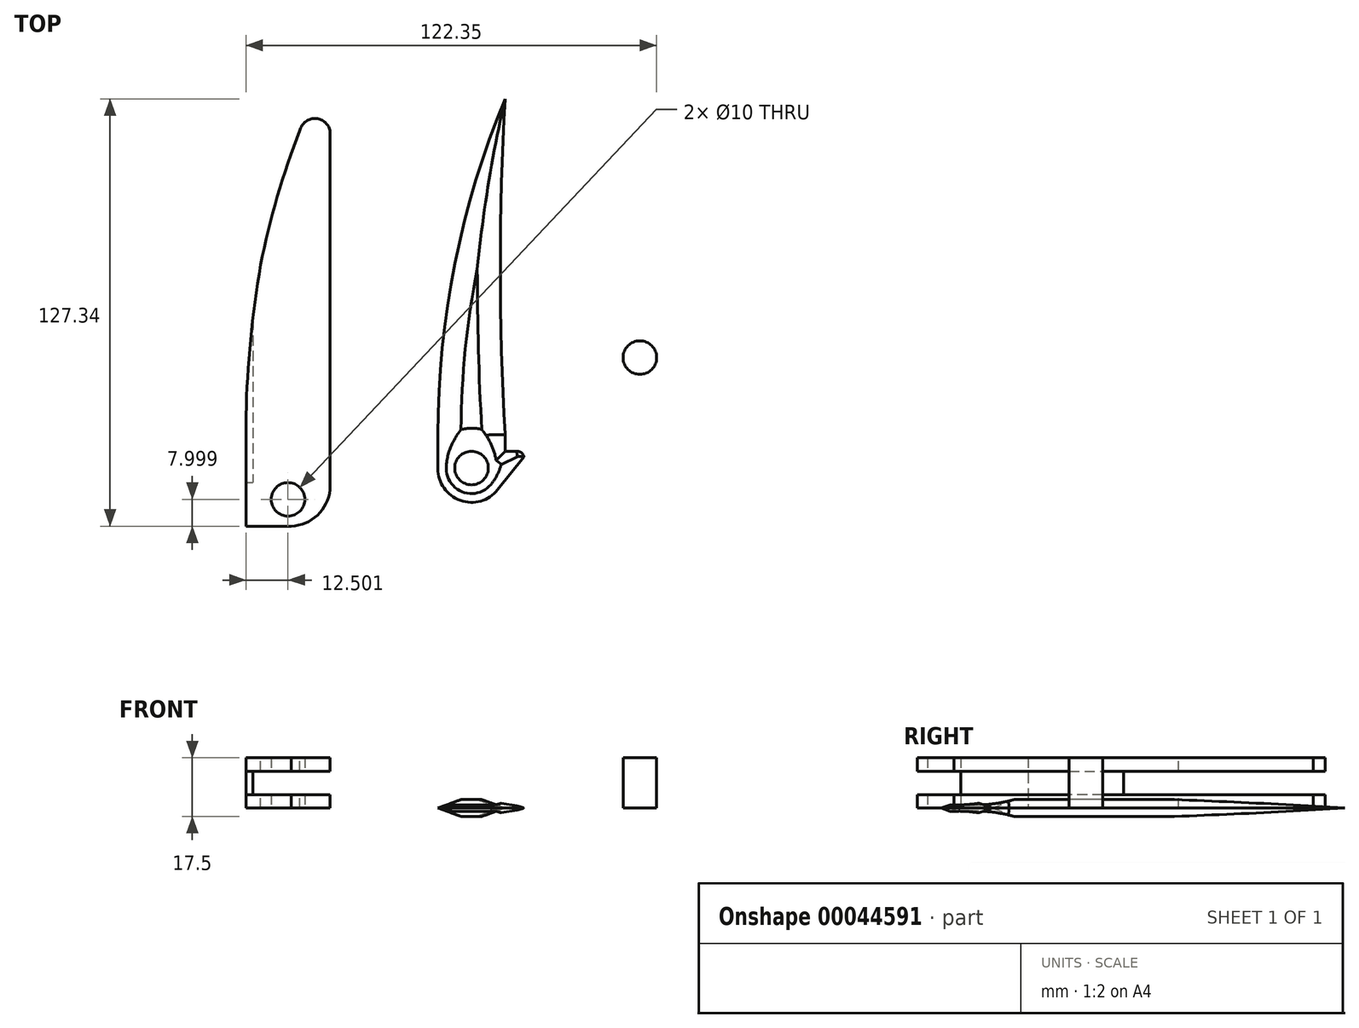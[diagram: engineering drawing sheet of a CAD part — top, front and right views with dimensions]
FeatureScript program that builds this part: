
annotation { "Feature Type Name" : "Feature", "Feature Type Description" : "" }
export const myFeature = defineFeature(function(context is Context, id is Id, definition is map)
    precondition{}
    {
        {
            var Q0;
            Q0=qCreatedBy(makeId("Top.planeOp"),FACE);
            var sketch = newSketch(context, id + "F0", { "sketchPlane" : qUnion([Q0])});
            skLineSegment(sketch, "E0.left", {"start": v(0, 0) * mm, "end": v(0, -5) * mm});
            skLineSegment(sketch, "E0.right", {"start": v(-20, 0) * mm, "end": v(-20, -10.3) * mm});
            skCircle(sketch, "E1", {"center": v(-10, -10) * mm, "radius": 5 * mm});
            skArc(sketch, "E2", {"start": v(-20, 0) * mm, "mid": v(-14.95, 51) * mm, "end": v(0, 100) * mm});
            skArc(sketch, "E3", {"start": v(0, 100) * mm, "mid": v(-1.43, 50) * mm, "end": v(0, 0) * mm});
            skArc(sketch, "E4", {"start": v(-20, -10.16) * mm, "mid": v(-13.34, -19.66) * mm, "end": v(-2.2, -16.48) * mm});
            skLineSegment(sketch, "E5", {"start": v(0, -5) * mm, "end": v(3.75, -5) * mm});
            skLineSegment(sketch, "E6", {"start": v(5.63, -6.7) * mm, "end": v(-2.2, -16.48) * mm});
            skArc(sketch, "E7", {"start": v(5.63, -6.7) * mm, "mid": v(4.9, -5.44) * mm, "end": v(3.5, -5) * mm});
            skPoint(sketch, "E8.orphan", {"position": v(7, -5) * mm});
            skPoint(sketch, "E9.orphan", {"position": v(-20, -20.33) * mm});
            skPoint(sketch, "E10.trimOffspring.end.orphan", {"position": v(0, -10) * mm});
            skPoint(sketch, "E11.trimOffspring.end.orphan", {"position": v(0, -20) * mm});
            skSolve(sketch);
        }
        {
            var Q0;
            Q0=qCreatedBy(makeId("Top.planeOp"),FACE);
            var sketch = newSketch(context, id + "F1", { "sketchPlane" : qUnion([Q0])});
            skLineSegment(sketch, "E12.bottom", {"start": v(-52.19, -34.34) * mm, "end": v(-77.19, -34.34) * mm});
            skLineSegment(sketch, "E12.top", {"start": v(-52.19, 85.66) * mm, "end": v(-77.19, 85.66) * mm});
            skLineSegment(sketch, "E12.left", {"start": v(-52.19, -34.34) * mm, "end": v(-52.19, 85.66) * mm});
            skLineSegment(sketch, "E12.right", {"start": v(-77.19, -34.34) * mm, "end": v(-77.19, 85.66) * mm});
            skCircle(sketch, "E13", {"center": v(-64.69, -19.34) * mm, "radius": 5 * mm});
            skArc(sketch, "E14", {"start": v(-64.69, 85.66) * mm, "mid": v(-74.63, 38.64) * mm, "end": v(-77.19, -9.34) * mm});
            skSolve(sketch);
        }
        {
            var Q0;
            {var subQ4=sQuery(id+"F1.wireOp",EDGE,"E12.bottom");Q0=makeQuery(id+"F1.imprint","IMPRINT",FACE,{"disambiguationData":[TD([[makeQuery(id+"F1.imprint","IMPRINT",EDGE,{"derivedFrom":subQ4}),-1.0]])]});}
            extrude(context, id + "F2", {"entities" : qUnion([Q0]), "depth" : 15 * mm});
        }
        {
            var Q0;
            Q0=makeQuery(id+"F2.opExtrude","SWEPT_FACE",FACE,{"disambiguationData":[OSD([sQuery(id+"F1.wireOp",EDGE,"E12.left")])]});
            var sketch = newSketch(context, id + "F3", { "sketchPlane" : qUnion([Q0])});
            skLineSegment(sketch, "E15", {"start": v(85.66, 4) * mm, "end": v(-34.34, 4) * mm});
            skLineSegment(sketch, "E16", {"start": v(-34.34, 11) * mm, "end": v(85.66, 11) * mm});
            skLineSegment(sketch, "E17", {"start": v(-34.34, 11) * mm, "end": v(-34.34, 4) * mm});
            skLineSegment(sketch, "E18", {"start": v(85.66, 11) * mm, "end": v(85.66, 4) * mm});
            skSolve(sketch);
        }
        {
            var Q0;
            Q0=makeQuery(id+"F3.imprint","IMPRINT",FACE,{"disambiguationData":[TD([[makeQuery(id+"F3.imprint","IMPRINT",EDGE,{"derivedFrom":sQuery(id+"F3.wireOp",EDGE,"E15")}),-1.0]])]});
            extrude(context, id + "F4", {"entities" : qUnion([Q0]), "operationType" : NewBodyOperationType.REMOVE, "oppositeDirection" : true, "depth" : 20 * mm});
        }
        {
            var Q0;
            Q0=qCreatedBy(makeId("Top.planeOp"),FACE);
            var sketch = newSketch(context, id + "F5", { "sketchPlane" : qUnion([Q0])});
            skCircle(sketch, "E19", {"center": v(40.16, 22.92) * mm, "radius": 5 * mm});
            skSolve(sketch);
        }
        {
            var Q0;
            Q0=makeQuery(id+"F5.imprint","IMPRINT",FACE,{"disambiguationData":[TD([[makeQuery(id+"F5.imprint","IMPRINT",EDGE,{"derivedFrom":sQuery(id+"F5.wireOp",EDGE,"E19")}),1.0]])]});
            extrude(context, id + "F6", {"entities" : qUnion([Q0]), "depth" : 15 * mm});
        }
        {
            var Q0;
            Q0=makeQuery(id+"F2.opExtrude","SWEPT_FACE",FACE,{"disambiguationData":[OSD([sQuery(id+"F1.wireOp",EDGE,"E12.bottom")])]});
            var sketch = newSketch(context, id + "F7", { "sketchPlane" : qUnion([Q0])});
            skLineSegment(sketch, "E20", {"start": v(-72.19, 11) * mm, "end": v(-77.19, 11) * mm});
            skLineSegment(sketch, "E21", {"start": v(-77.19, 11) * mm, "end": v(-77.19, 4) * mm});
            skLineSegment(sketch, "E22", {"start": v(-77.19, 4) * mm, "end": v(-72.19, 4) * mm});
            skLineSegment(sketch, "E23", {"start": v(-72.19, 4) * mm, "end": v(-72.19, 11) * mm});
            skSolve(sketch);
        }
        {
            var Q0;
            Q0 = qSketchRegion(id + "F7", true);
            extrude(context, id + "F8", {"entities" : qUnion([Q0]), "operationType" : NewBodyOperationType.REMOVE, "oppositeDirection" : true, "depth" : 15 * mm});
        }
        {
            var Q0;
            Q0 = qSketchRegion(id + "F0", true);
            var Q1;
            {var subQ10=sQuery(id+"F0.wireOp",EDGE,"E0.left");Q1=makeQuery(id+"F0.imprint","IMPRINT",FACE,{"disambiguationData":[TD([[makeQuery(id+"F0.imprint","IMPRINT",EDGE,{"derivedFrom":subQ10}),-1.0]])]});}
            extrude(context, id + "F9", {"entities" : qUnion([Q0, Q1]), "endBound" : BoundingType.SYMMETRIC, "depth" : 5 * mm, "hasDraft" : true, "draftAngle" : 70 * degree, "draftPullDirection" : true});
        }
        {
            var Q0;
            Q0=makeQuery(id+"F4.boolean.opBoolean","COPY",FACE,{"derivedFrom":makeQuery(id+"F4.opExtrude","CAP_FACE",FACE,{"disambiguationData":[OSD([sQuery(id+"F3.wireOp",EDGE,"E15"),sQuery(id+"F3.wireOp",EDGE,"E16"),sQuery(id+"F3.wireOp",EDGE,"E17"),sQuery(id+"F3.wireOp",EDGE,"E18")])],"isStart":false})});
            extrude(context, id + "F10", {"entities" : qUnion([Q0]), "operationType" : NewBodyOperationType.REMOVE, "oppositeDirection" : true, "depth" : 3 * mm});
        }
        {
            var Q0;
            {var subQ0=sQuery(id+"F1.wireOp",EDGE,"E12.bottom");Q0=makeQuery(id+"F8.boolean.opBoolean","SPLIT",FACE,{"disambiguationData":[TD([makeQuery(id+"F4.boolean.opBoolean","COPY",FACE,{"derivedFrom":makeQuery(id+"F4.opExtrude","SWEPT_FACE",FACE,{"disambiguationData":[OSD([sQuery(id+"F3.wireOp",EDGE,"E16")])]})})])],"derivedFrom":makeQuery(id+"F2.opExtrude","SWEPT_FACE",FACE,{"disambiguationData":[OSD([subQ0])]})});}
            var Q1;
            {var subQ0=sQuery(id+"F1.wireOp",EDGE,"E12.bottom");Q1=makeQuery(id+"F8.boolean.opBoolean","SPLIT",FACE,{"disambiguationData":[TD([makeQuery(id+"F4.boolean.opBoolean","COPY",FACE,{"derivedFrom":makeQuery(id+"F4.opExtrude","SWEPT_FACE",FACE,{"disambiguationData":[OSD([sQuery(id+"F3.wireOp",EDGE,"E15")])]})})])],"derivedFrom":makeQuery(id+"F2.opExtrude","SWEPT_FACE",FACE,{"disambiguationData":[OSD([subQ0])]})});}
            var Q2;
            Q2=makeQuery(id+"F8.boolean.opBoolean","COPY",FACE,{"derivedFrom":makeQuery(id+"F8.opExtrude","CAP_FACE",FACE,{"disambiguationData":[OSD([sQuery(id+"F7.wireOp",EDGE,"E20"),sQuery(id+"F7.wireOp",EDGE,"E21"),sQuery(id+"F7.wireOp",EDGE,"E22"),sQuery(id+"F7.wireOp",EDGE,"E23")])],"isStart":false})});
            extrude(context, id + "F11", {"entities" : qUnion([Q0, Q1, Q2]), "operationType" : NewBodyOperationType.REMOVE, "oppositeDirection" : true, "depth" : 7 * mm});
        }
        {
            var Q0;
            {var subQ0=sQuery(id+"F1.wireOp",EDGE,"E12.top");Q0=makeQuery(id+"F4.boolean.opBoolean","SPLIT",FACE,{"disambiguationData":[TD([makeQuery(id+"F4.opExtrude","SWEPT_FACE",FACE,{"disambiguationData":[OSD([sQuery(id+"F3.wireOp",EDGE,"E15")])]})])],"derivedFrom":makeQuery(id+"F2.opExtrude","SWEPT_FACE",FACE,{"disambiguationData":[OSD([subQ0])]})});}
            var Q1;
            {var subQ0=sQuery(id+"F1.wireOp",EDGE,"E12.top");Q1=makeQuery(id+"F4.boolean.opBoolean","SPLIT",FACE,{"disambiguationData":[TD([makeQuery(id+"F4.opExtrude","SWEPT_FACE",FACE,{"disambiguationData":[OSD([sQuery(id+"F3.wireOp",EDGE,"E16")])]})])],"derivedFrom":makeQuery(id+"F2.opExtrude","SWEPT_FACE",FACE,{"disambiguationData":[OSD([subQ0])]})});}
            extrude(context, id + "F12", {"entities" : qUnion([Q0, Q1]), "operationType" : NewBodyOperationType.ADD, "depth" : 25 * mm});
        }
        {
            var Q0;
            {var subQ0=sQuery(id+"F1.wireOp",EDGE,"E12.top");Q0=makeQuery(id+"F12.boolean.opBoolean","MERGE",FACE,{"derivedFrom":[makeQuery(id+"F2.opExtrude","CAP_FACE",FACE,{"disambiguationData":[OSD([sQuery(id+"F1.wireOp",EDGE,"E12.bottom"),subQ0,sQuery(id+"F1.wireOp",EDGE,"E12.left"),sQuery(id+"F1.wireOp",EDGE,"E12.right"),sQuery(id+"F1.wireOp",EDGE,"E13"),sQuery(id+"F1.wireOp",EDGE,"E14")])],"isStart":false}),makeQuery(id+"F12.opExtrude","SWEPT_FACE",FACE,{"disambiguationData":[OSD([subQ0]),TDD([makeQuery(id+"F2.opExtrude","CAP_EDGE",EDGE,{"disambiguationData":[OSD([subQ0])],"isStart":false})])]})]});}
            var sketch = newSketch(context, id + "F13", { "sketchPlane" : qUnion([Q0])});
            skArc(sketch, "E24", {"start": v(-52.19, 110.66) * mm, "mid": v(-70.85, 59.64) * mm, "end": v(-77.19, 5.69) * mm});
            skLineSegment(sketch, "E25", {"start": v(-52.19, 110.66) * mm, "end": v(-52.19, 90.66) * mm});
            skArc(sketch, "E26", {"start": v(-52.19, 90.66) * mm, "mid": v(-56.66, 94.2) * mm, "end": v(-61.13, 90.66) * mm});
            skSolve(sketch);
        }
        {
            var Q0;
            {var subQ4=sQuery(id+"F1.wireOp",EDGE,"E12.top");var subQ6=makeQuery(id+"F12.opExtrude","CAP_EDGE",EDGE,{"disambiguationData":[OSD([subQ4]),TDD([makeQuery(id+"F2.opExtrude","CAP_EDGE",EDGE,{"disambiguationData":[OSD([subQ4])],"isStart":false})])],"isStart":false});Q0=makeQuery(id+"F13.imprint","IMPRINT",FACE,{"disambiguationData":[TD([[makeQuery(id+"F13.imprint","IMPRINT",EDGE,{"derivedFrom":subQ6}),1.0]])]});}
            extrude(context, id + "F14", {"entities" : qUnion([Q0]), "operationType" : NewBodyOperationType.REMOVE, "oppositeDirection" : true, "depth" : 25 * mm});
        }
        {
            var Q0;
            {var subQ5=sQuery(id+"F13.wireOp",EDGE,"E25");Q0=makeQuery(id+"F13.imprint","IMPRINT",FACE,{"disambiguationData":[TD([[makeQuery(id+"F13.imprint","IMPRINT",EDGE,{"derivedFrom":subQ5}),1.0]])]});}
            var Q1;
            {var subQ3=sQuery(id+"F1.wireOp",EDGE,"E12.top");var subQ4=makeQuery(id+"F12.opExtrude","CAP_EDGE",EDGE,{"disambiguationData":[OSD([subQ3]),TDD([makeQuery(id+"F2.opExtrude","CAP_EDGE",EDGE,{"disambiguationData":[OSD([subQ3])],"isStart":false})])],"isStart":false});Q1=makeQuery(id+"F13.imprint","IMPRINT",FACE,{"disambiguationData":[TD([[makeQuery(id+"F13.imprint","IMPRINT",EDGE,{"derivedFrom":subQ4}),1.0]])]});}
            extrude(context, id + "F15", {"entities" : qUnion([Q0, Q1]), "operationType" : NewBodyOperationType.REMOVE, "oppositeDirection" : true, "depth" : 25 * mm});
        }
        {
            var Q0;
            {var subQ0=sQuery(id+"F1.wireOp",EDGE,"E12.top");Q0=makeQuery(id+"F12.boolean.opBoolean","MERGE",FACE,{"derivedFrom":[makeQuery(id+"F2.opExtrude","CAP_FACE",FACE,{"disambiguationData":[OSD([sQuery(id+"F1.wireOp",EDGE,"E12.bottom"),subQ0,sQuery(id+"F1.wireOp",EDGE,"E12.left"),sQuery(id+"F1.wireOp",EDGE,"E12.right"),sQuery(id+"F1.wireOp",EDGE,"E13"),sQuery(id+"F1.wireOp",EDGE,"E14")])],"isStart":false}),makeQuery(id+"F12.opExtrude","SWEPT_FACE",FACE,{"disambiguationData":[OSD([subQ0]),TDD([makeQuery(id+"F2.opExtrude","CAP_EDGE",EDGE,{"disambiguationData":[OSD([subQ0])],"isStart":false})])]})]});}
            var sketch = newSketch(context, id + "F16", { "sketchPlane" : qUnion([Q0])});
            skLineSegment(sketch, "E27", {"start": v(-64.65, -24.34) * mm, "end": v(-64.65, -27.34) * mm});
            skArc(sketch, "E28", {"start": v(-64.65, -27.34) * mm, "mid": v(-56.26, -24.38) * mm, "end": v(-52.19, -16.48) * mm});
            skLineSegment(sketch, "E29", {"start": v(-52.19, -16.48) * mm, "end": v(-52.19, -27.34) * mm});
            skLineSegment(sketch, "E30", {"start": v(-52.19, -27.34) * mm, "end": v(-64.65, -27.34) * mm});
            skSolve(sketch);
        }
        {
            var Q0;
            {var subQ3=sQuery(id+"F16.wireOp",EDGE,"E29");Q0=makeQuery(id+"F16.imprint","IMPRINT",FACE,{"disambiguationData":[TD([[makeQuery(id+"F16.imprint","IMPRINT",EDGE,{"derivedFrom":subQ3}),1.0]])]});}
            extrude(context, id + "F17", {"entities" : qUnion([Q0]), "operationType" : NewBodyOperationType.REMOVE, "oppositeDirection" : true, "depth" : 25 * mm});
        }
        {
            var Q0;
            Q0=makeQuery(id+"F11.boolean.opBoolean","COPY",FACE,{"derivedFrom":makeQuery(id+"F11.opExtrude","CAP_FACE",FACE,{"disambiguationData":[OSD([sQuery(id+"F7.wireOp",EDGE,"E20"),sQuery(id+"F7.wireOp",EDGE,"E21"),sQuery(id+"F7.wireOp",EDGE,"E22"),sQuery(id+"F7.wireOp",EDGE,"E23")])],"isStart":false})});
            extrude(context, id + "F18", {"entities" : qUnion([Q0]), "operationType" : NewBodyOperationType.ADD, "depth" : 2 * mm});
        }
    });
